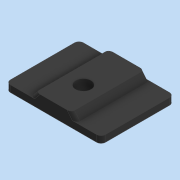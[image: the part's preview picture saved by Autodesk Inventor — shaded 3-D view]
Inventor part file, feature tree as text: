
AUTODESK INVENTOR PART (.ipt)
format: ipt  version: 2020 (Build 240168000, 168)  size: 273,920 bytes
history: native  units: mm
features: extrude x3, fillet x2, sketch x2, other x1, pattern_linear x1, mirror x1
ambient origin geometry x8: Origin, YZ Plane, XZ Plane, XY Plane, X Axis, Y Axis, Z Axis, Center Point
bodies: Body1 (feature_tree)
feature tree (10):
  other  "實體1"
  extrude  "擠出1"  Depth=3.0mm
  fillet  "圓角1"  Radius=16.0mm
  fillet  "圓角2"  Radius=43.0mm
  extrude  "擠出3"  Depth=11.0mm
  pattern_linear  "矩形陣列1"  Spacing1=6.0mm  [1 undecoded]
  mirror  "鏡射1"
  extrude  "擠出4"  Depth=33.0mm TaperAngle=0.0deg
  sketch  "草圖3"
  sketch  "草圖4"
note: 1 required parameter value undecoded (feature->parameter linkage not recoverable at this tier; creation-order binding heuristic only, values carry confidence <= 0.55)
